# Revit family: ARKOSLIGHT_Divi direct initial
name_source: partatom
category: Luminarias
units: mm (PartAtom-declared; Revit-internal decimal feet)

## family parameters
Anfitrión = Cara
Compartido = No
Corte con vacíos al cargar = No
Cota de conector redondo = Diámetro de uso
Origen de luz = No
Punto de cálculo de habitación = No
Tipo de pieza = Normal

## types (2) — shared parameters
ARKOSLIGHT_Apparent Load = 14 VA
ARKOSLIGHT_Beam Angle = 115.00°
ARKOSLIGHT_CCT = 3000 K
ARKOSLIGHT_CRI = CRI>90
ARKOSLIGHT_Dimming = No Dim / DALI / Push
ARKOSLIGHT_Fixture Type = CUSTOM SYSTEMS
ARKOSLIGHT_IP = 20
ARKOSLIGHT_Luminous flux = 1650 lm
ARKOSLIGHT_Model = DIVI
ARKOSLIGHT_Series = DIVI DIRECT MODULE
Carga aparente = 14 VA
Fabricante = ARKOSLIGHT
Modelo = DIVI
URL = https://www.arkoslight.com
zero-valued in all types: Elevación por defecto

## per-type parameters (varying)
| type | ARKOSLIGHT_Body_Color | ARKOSLIGHT_Body_Secondary_Color | ARKOSLIGHT_Cable_Color | ARKOSLIGHT_Cable_Electric_Color | ARKOSLIGHT_Color | ARKOSLIGHT_Efficiency | ARKOSLIGHT_IES | ARKOSLIGHT_Reference | IES |
| A5380101NT - DIVI DIRECT INITIAL 3000K NT | ARKOSLIGHT_Textured black | ARKOSLIGHT_Black | ARKOSLIGHT_Black | ARKOSLIGHT_Black | Textured black | 51% | A538-01-0-1-NT DIVI DIRECT INITIAL 3000K CRI90.ies | A5380101NT | IES : A5380101NT - DIVI DIRECT INITIAL 3000K NT |
| A5380101WT - DIVI DIRECT INITIAL 3000K WT | ARKOSLIGHT_Textured white | ARKOSLIGHT_White | ARKOSLIGHT_White | ARKOSLIGHT_Steel | Textured white | 58% | A538-01-0-1-WT DIVI DIRECT INITIAL 3000K CRI90.ies | A5380101WT | IES : A5380101WT - DIVI DIRECT INITIAL 3000K WT |

## geometry (parser evidence)
native form markers: Sweep x13
no freeform markers — native parametric forms only
